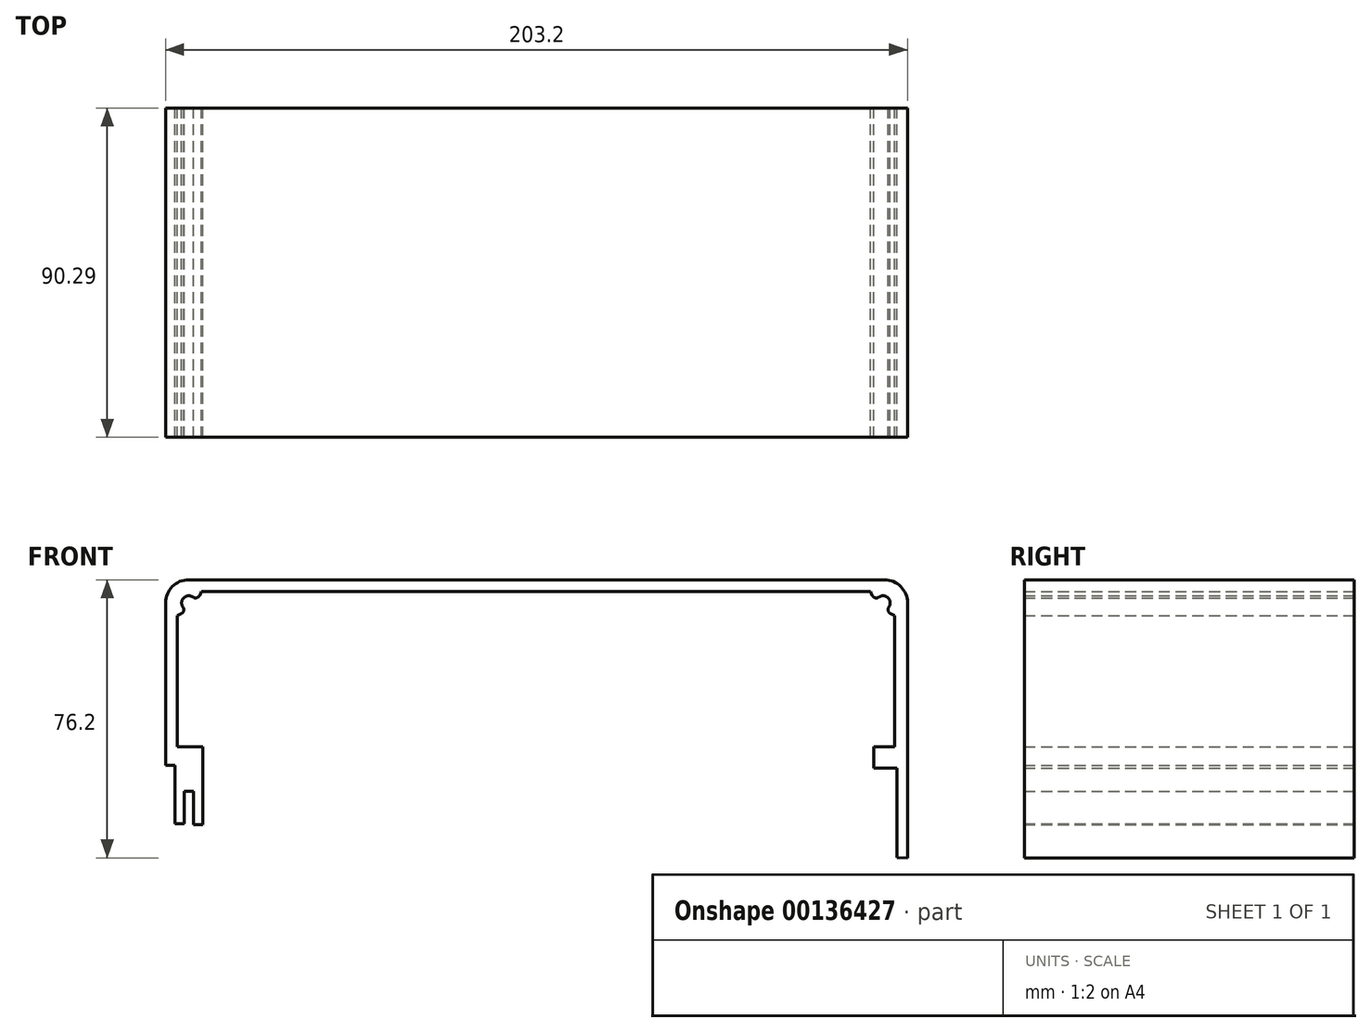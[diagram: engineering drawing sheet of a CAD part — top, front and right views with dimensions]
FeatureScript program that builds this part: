
annotation { "Feature Type Name" : "Feature", "Feature Type Description" : "" }
export const myFeature = defineFeature(function(context is Context, id is Id, definition is map)
    precondition{}
    {
        {
            var Q0;
            Q0=qCreatedBy(makeId("Front.planeOp"),FACE);
            var sketch = newSketch(context, id + "F0", { "sketchPlane" : qUnion([Q0])});
            skLineSegment(sketch, "E0", {"start": v(-95.08, 53.75) * mm, "end": v(95.42, 53.75) * mm});
            skPoint(sketch, "E1", {"position": v(0, 53.75) * mm});
            skLineSegment(sketch, "E2", {"start": v(-101.43, 47.4) * mm, "end": v(-101.43, 2.95) * mm});
            skLineSegment(sketch, "E3", {"start": v(101.77, 47.4) * mm, "end": v(101.77, -22.45) * mm});
            skPoint(sketch, "E4.visualSharp", {"position": v(-101.43, 53.75) * mm});
            skArc(sketch, "E4.filletArc", {"start": v(-95.08, 53.75) * mm, "mid": v(-99.57, 51.9) * mm, "end": v(-101.43, 47.4) * mm});
            skPoint(sketch, "E5.visualSharp", {"position": v(101.77, 53.75) * mm});
            skArc(sketch, "E5.filletArc", {"start": v(101.77, 47.4) * mm, "mid": v(99.9, 51.9) * mm, "end": v(95.42, 53.75) * mm});
            skLineSegment(sketch, "E6", {"start": v(-101.43, 2.95) * mm, "end": v(-98.9, 2.95) * mm});
            skLineSegment(sketch, "E7", {"start": v(-98.9, 2.95) * mm, "end": v(-98.9, -13.1) * mm});
            skLineSegment(sketch, "E8", {"start": v(-98.9, -13.1) * mm, "end": v(-96.35, -13.1) * mm});
            skLineSegment(sketch, "E9", {"start": v(-96.35, -13.1) * mm, "end": v(-96.35, -4.16) * mm});
            skLineSegment(sketch, "E10", {"start": v(-96.35, -4.16) * mm, "end": v(-93.81, -4.16) * mm});
            skLineSegment(sketch, "E11", {"start": v(-93.81, -4.16) * mm, "end": v(-93.81, -13.32) * mm});
            skLineSegment(sketch, "E12", {"start": v(-93.81, -13.32) * mm, "end": v(-91.27, -13.32) * mm});
            skLineSegment(sketch, "E13", {"start": v(-91.27, -13.32) * mm, "end": v(-91.27, 7.93) * mm});
            skLineSegment(sketch, "E14", {"start": v(-91.27, 7.93) * mm, "end": v(-98.26, 7.93) * mm});
            skLineSegment(sketch, "E15", {"start": v(-98.26, 7.93) * mm, "end": v(-98.26, 43.91) * mm});
            skArc(sketch, "E16", {"start": v(-93.16, 47.09) * mm, "mid": v(-96.46, 48.78) * mm, "end": v(-94.77, 45.48) * mm});
            skLineSegment(sketch, "E17", {"start": v(-98.26, 43.91) * mm, "end": v(-94.77, 45.48) * mm});
            skLineSegment(sketch, "E18", {"start": v(-95.08, 47.4) * mm, "end": v(-101.43, 53.75) * mm, "construction": true});
            skLineSegment(sketch, "E19.MirrorCS", {"start": v(-91.6, 50.58) * mm, "end": v(-93.16, 47.09) * mm});
            skLineSegment(sketch, "E20", {"start": v(0, 53.75) * mm, "end": v(0, 0) * mm, "construction": true});
            skLineSegment(sketch, "E21.MirrorCS", {"start": v(98.26, 43.91) * mm, "end": v(94.77, 45.48) * mm});
            skArc(sketch, "E22.MirrorC", {"start": v(93.16, 47.09) * mm, "mid": v(96.46, 48.78) * mm, "end": v(94.77, 45.48) * mm});
            skLineSegment(sketch, "E23.MirrorCS", {"start": v(91.6, 50.58) * mm, "end": v(93.16, 47.09) * mm});
            skLineSegment(sketch, "E24.MirrorCS", {"start": v(98.26, 7.93) * mm, "end": v(98.26, 43.91) * mm});
            skLineSegment(sketch, "E25", {"start": v(-91.6, 50.58) * mm, "end": v(91.6, 50.58) * mm});
            skLineSegment(sketch, "E26", {"start": v(98.26, 7.93) * mm, "end": v(92.5, 7.93) * mm});
            skLineSegment(sketch, "E27", {"start": v(92.5, 7.93) * mm, "end": v(92.5, 2.18) * mm});
            skLineSegment(sketch, "E28", {"start": v(92.5, 2.18) * mm, "end": v(98.9, 2.18) * mm});
            skLineSegment(sketch, "E29", {"start": v(98.9, 2.18) * mm, "end": v(98.9, -22.32) * mm});
            skLineSegment(sketch, "E30", {"start": v(98.9, -22.32) * mm, "end": v(101.77, -22.45) * mm});
            skSolve(sketch);
        }
        {
            var Q0;
            Q0=makeQuery(id+"F0.imprint","IMPRINT",FACE,{"disambiguationData":[TD([[makeQuery(id+"F0.imprint","IMPRINT",EDGE,{"derivedFrom":sQuery(id+"F0.wireOp",EDGE,"E0")}),-1.0]])]});
            extrude(context, id + "F1", {"entities" : qUnion([Q0]), "depth" : 90.3 * mm});
        }
        {
            var Q0;
            Q0=makeQuery(id+"F1.opExtrude","SWEPT_EDGE",EDGE,{"disambiguationData":[OSD([sQuery(id+"F0.wireOp",EDGE,"E16"),sQuery(id+"F0.wireOp",EDGE,"E17")])]});
            var Q1;
            Q1=makeQuery(id+"F1.opExtrude","SWEPT_EDGE",EDGE,{"disambiguationData":[OSD([sQuery(id+"F0.wireOp",EDGE,"E16"),sQuery(id+"F0.wireOp",EDGE,"E19.MirrorCS")])]});
            var Q2;
            Q2=makeQuery(id+"F1.opExtrude","SWEPT_EDGE",EDGE,{"disambiguationData":[OSD([sQuery(id+"F0.wireOp",EDGE,"E22.MirrorC"),sQuery(id+"F0.wireOp",EDGE,"E23.MirrorCS")])]});
            var Q3;
            Q3=makeQuery(id+"F1.opExtrude","SWEPT_EDGE",EDGE,{"disambiguationData":[OSD([sQuery(id+"F0.wireOp",EDGE,"E21.MirrorCS"),sQuery(id+"F0.wireOp",EDGE,"E22.MirrorC")])]});
            fillet(context, id + "F2", {"entities" : qUnion([Q0, Q1, Q2, Q3]), "radius" : 1.27 * mm, "tangentPropagation" : true, "allowEdgeOverflow" : false});
        }
    });
